# Revit family: Malvestio_Itala-
name_source: partatom
category: Furniture
revit_build: Autodesk Revit 2018 (Build: 20190510_1515(x64)
units: mm (PartAtom-declared; Revit-internal decimal feet)

## family parameters
Always vertical = Yes
Cut with Voids When Loaded = No
OmniClass Number = 23.40.20.17.14.11
OmniClass Title = Beds
Room Calculation Point = No
Shared = No
Work Plane-Based = No

## types (2) — shared parameters
Bed_H Max = 890 mm
Bed_H Min = 560 mm  [stored 1.83727 ft]
Bed_Inc Max = 17.00°
Bed_Inc Min = -17.00°
DIM_Depth = 827 mm
DIM_Height = 1300 mm  [stored 4.26509 ft]
DIM_Mattress_Thick = 150 mm
DIM_Width = 2107 mm  [stored 6.91273 ft]
Frame_Base offset = 190 mm  [stored 0.62336 ft]
Keynote = 0
Manufacturer = Malvestio Spa
Mat_Aluminum = Aluminum
Mat_Bump = Rubber Gray
Mat_Bump_SideRail = Rubber Black
Mat_Case = RAL 9010
Mat_Panel = RAL 9010
Mat_Side Rail_HeadFoot = Rubber Black
Mat_Weel_Tyre = Rubber Black
Product Disclaimer = Malvestio Spa declines any responsibility for
the modifications of the type parameters.
The company is not responsible for the
objects/drawings and the correct
production/installation.
The company reserves the right to make technical
improvements or modifications of any type without
prior notice to the customer.
All rights reserved.
Product Series = Itala
Product URL = https://www.malvestio.com
URL = https://www.malvestio.com
Weight = 120.00 kg

## per-type parameters (varying)
| type | Back_Grid | Back_Panel |
| 320760 | Yes | No |
| 320760RX | No | Yes |

note: column(s) folded — value = type name in every type: Model, Product Code, Product Model

note: [stored X ft] marks values corroborated as IEEE doubles in the binary element streams (Revit-internal decimal feet)

## geometry (parser evidence)
native form markers: Sweep x9
no freeform markers — native parametric forms only
